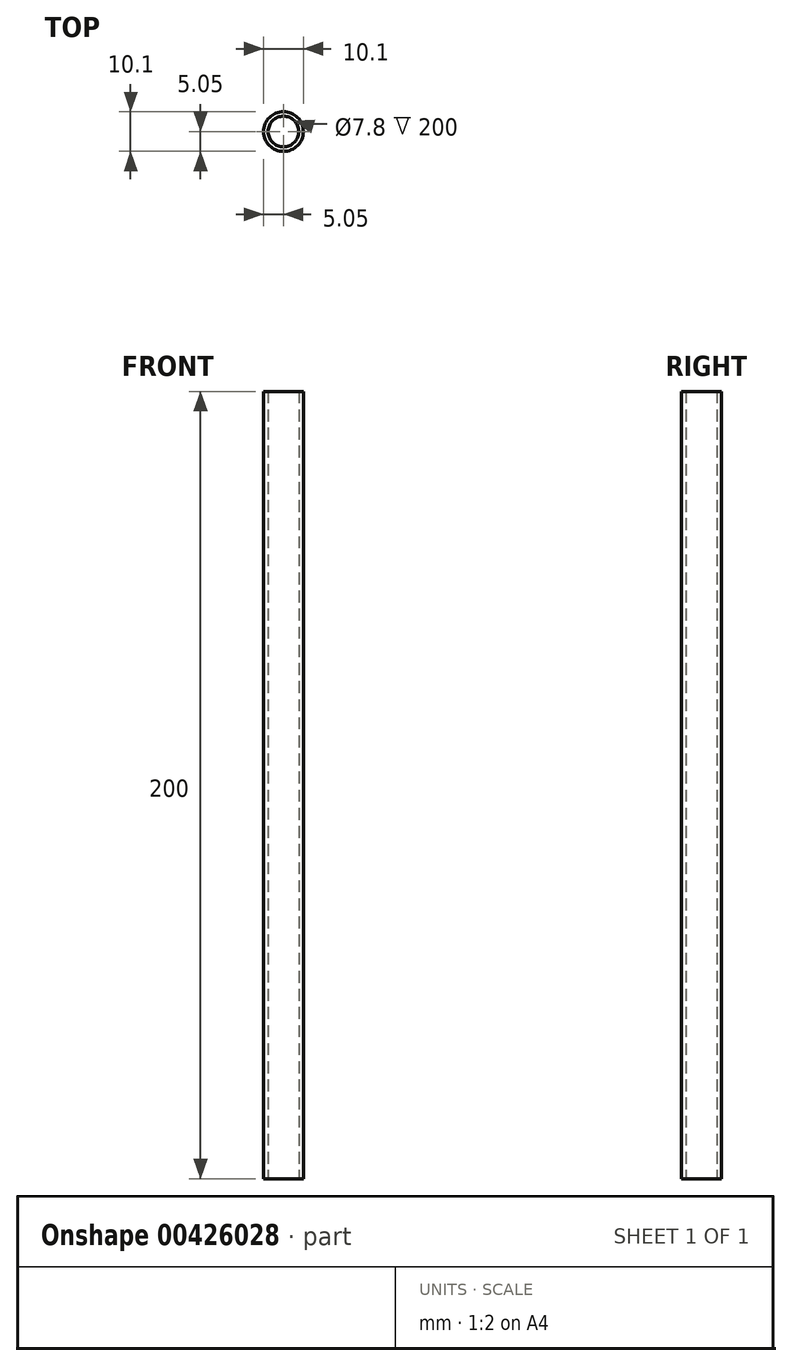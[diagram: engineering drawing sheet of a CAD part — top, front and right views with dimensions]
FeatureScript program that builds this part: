
annotation { "Feature Type Name" : "Feature", "Feature Type Description" : "" }
export const myFeature = defineFeature(function(context is Context, id is Id, definition is map)
    precondition{}
    {
        {
            var Q0;
            Q0=qCreatedBy(makeId("Top.planeOp"),FACE);
            var sketch = newSketch(context, id + "F0", { "sketchPlane" : qUnion([Q0])});
            skCircle(sketch, "E0", {"center": v(0, 0) * mm, "radius": 3.9 * mm});
            skCircle(sketch, "E1", {"center": v(0, 0) * mm, "radius": 5.05 * mm});
            skSolve(sketch);
        }
        {
            var Q0;
            Q0=makeQuery(id+"F0.imprint","IMPRINT",FACE,{"disambiguationData":[TD([[makeQuery(id+"F0.imprint","IMPRINT",EDGE,{"derivedFrom":sQuery(id+"F0.wireOp",EDGE,"E0")}),-1.0]])]});
            extrude(context, id + "F1", {"entities" : qUnion([Q0]), "depth" : 100 * mm, "offsetDistance" : 25 * mm, "hasSecondDirection" : true, "secondDirectionOppositeDirection" : true, "secondDirectionDepth" : 100 * mm});
        }
    });
